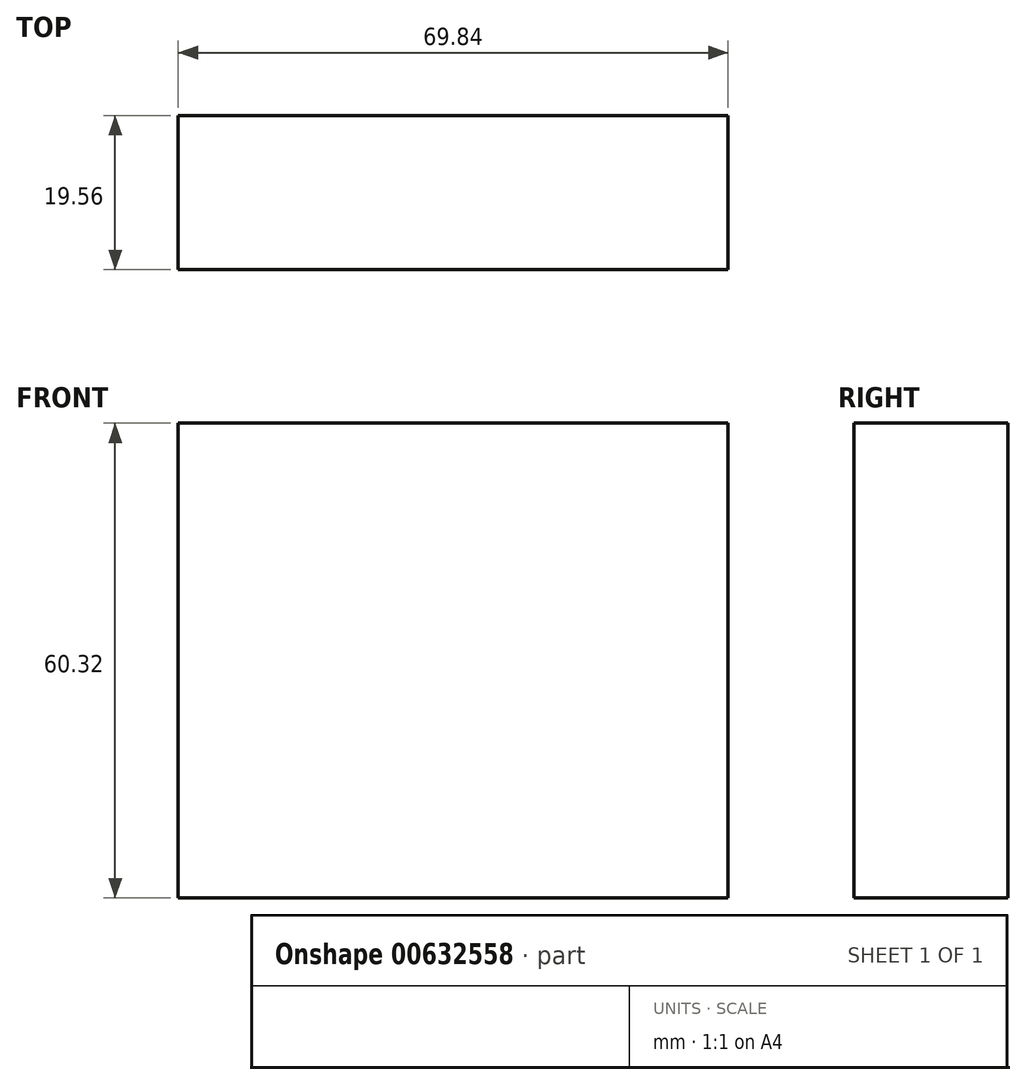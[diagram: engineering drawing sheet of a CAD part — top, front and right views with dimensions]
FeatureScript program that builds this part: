
annotation { "Feature Type Name" : "Feature", "Feature Type Description" : "" }
export const myFeature = defineFeature(function(context is Context, id is Id, definition is map)
    precondition{}
    {
        {
            var Q0;
            Q0=qCreatedBy(makeId("Front.planeOp"),FACE);
            var sketch = newSketch(context, id + "F0", { "sketchPlane" : qUnion([Q0])});
            skLineSegment(sketch, "E0.bottom", {"start": v(34.93, -30.16) * mm, "end": v(-34.92, -30.16) * mm});
            skLineSegment(sketch, "E0.top", {"start": v(34.92, 30.16) * mm, "end": v(-34.93, 30.16) * mm});
            skLineSegment(sketch, "E0.left", {"start": v(34.93, -30.16) * mm, "end": v(34.92, 30.16) * mm});
            skLineSegment(sketch, "E0.right", {"start": v(-34.92, -30.16) * mm, "end": v(-34.93, 30.16) * mm});
            skPoint(sketch, "E0.middle", {"position": v(0, 0) * mm});
            skSolve(sketch);
        }
        {
            var Q0;
            Q0 = qSketchRegion(id + "F0", true);
            extrude(context, id + "F1", {"entities" : qUnion([Q0]), "depth" : 19.56 * mm, "offsetDistance" : 25.4 * mm});
        }
    });
